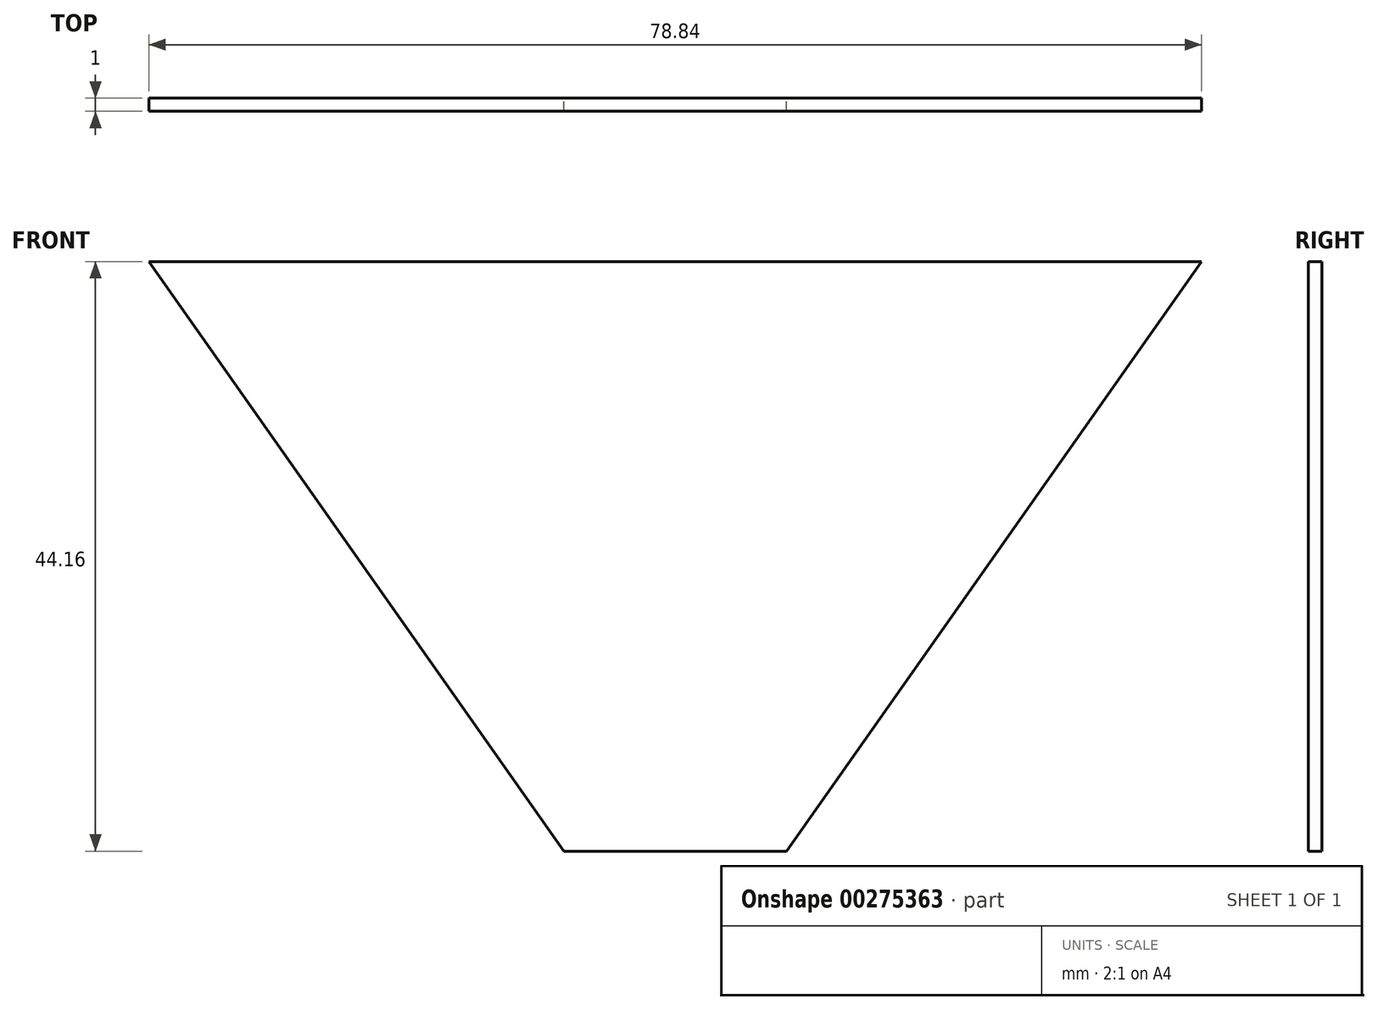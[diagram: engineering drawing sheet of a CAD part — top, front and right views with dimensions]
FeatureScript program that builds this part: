
annotation { "Feature Type Name" : "Feature", "Feature Type Description" : "" }
export const myFeature = defineFeature(function(context is Context, id is Id, definition is map)
    precondition{}
    {
        {
            var Q0;
            Q0=qCreatedBy(makeId("Front.planeOp"),FACE);
            var sketch = newSketch(context, id + "F0", { "sketchPlane" : qUnion([Q0])});
            skLineSegment(sketch, "E0", {"start": v(-30.75, 35.16) * mm, "end": v(30.75, 35.16) * mm, "construction": true});
            skLineSegment(sketch, "E1", {"start": v(30.75, 35.16) * mm, "end": v(6, 0) * mm, "construction": true});
            skLineSegment(sketch, "E2", {"start": v(6, 0) * mm, "end": v(-6, 0) * mm, "construction": true});
            skLineSegment(sketch, "E3", {"start": v(-6, 0) * mm, "end": v(-30.75, 35.16) * mm, "construction": true});
            skLineSegment(sketch, "E4.0", {"start": v(-39.42, 39.66) * mm, "end": v(39.42, 39.66) * mm});
            skLineSegment(sketch, "E4.1", {"start": v(-8.34, -4.5) * mm, "end": v(-39.42, 39.66) * mm});
            skLineSegment(sketch, "E4.2", {"start": v(8.34, -4.5) * mm, "end": v(-8.34, -4.5) * mm});
            skLineSegment(sketch, "E4.3", {"start": v(39.42, 39.66) * mm, "end": v(8.34, -4.5) * mm});
            skSolve(sketch);
        }
        {
            var Q0;
            Q0=makeQuery(id+"F0.imprint","IMPRINT",FACE,{"disambiguationData":[TD([[makeQuery(id+"F0.imprint","IMPRINT",EDGE,{"derivedFrom":sQuery(id+"F0.wireOp",EDGE,"E4.0")}),-1.0]])]});
            extrude(context, id + "F1", {"entities" : qUnion([Q0]), "depth" : 1 * mm});
        }
    });
